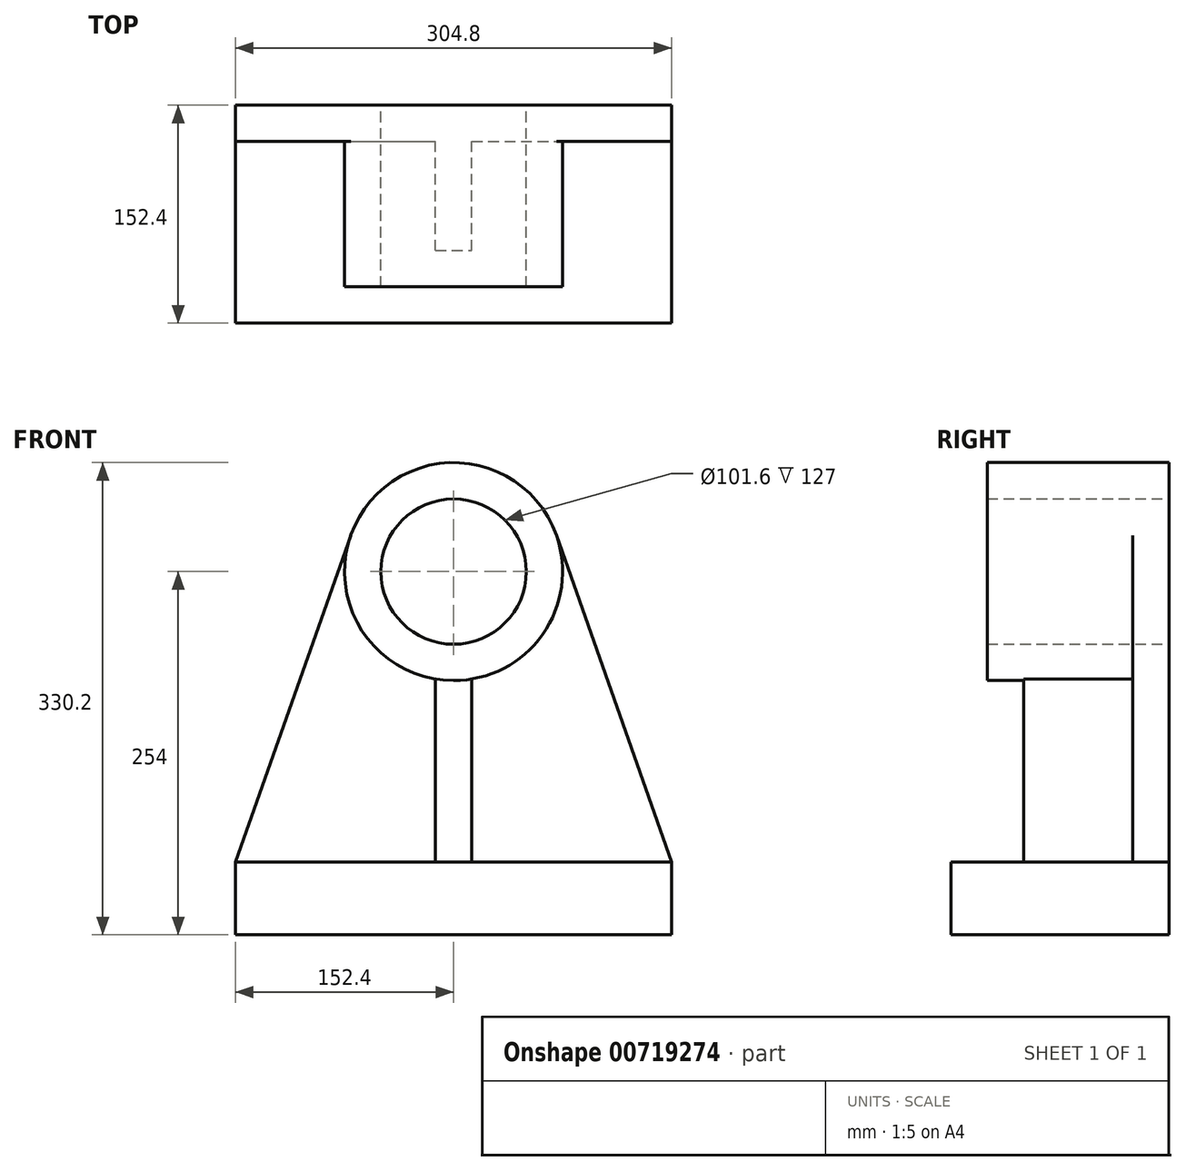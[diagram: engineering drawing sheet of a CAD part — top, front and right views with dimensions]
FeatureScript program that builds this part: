
annotation { "Feature Type Name" : "Feature", "Feature Type Description" : "" }
export const myFeature = defineFeature(function(context is Context, id is Id, definition is map)
    precondition{}
    {
        {
            var Q0;
            Q0=qCreatedBy(makeId("Front.planeOp"),FACE);
            var sketch = newSketch(context, id + "F0", { "sketchPlane" : qUnion([Q0])});
            skCircle(sketch, "E0", {"center": v(0, 0) * mm, "radius": 76.2 * mm});
            skCircle(sketch, "E1", {"center": v(0, 0) * mm, "radius": 50.8 * mm});
            skSolve(sketch);
        }
        {
            var Q0;
            Q0=makeQuery(id+"F0.imprint","IMPRINT",FACE,{"disambiguationData":[TD([[makeQuery(id+"F0.imprint","IMPRINT",EDGE,{"derivedFrom":sQuery(id+"F0.wireOp",EDGE,"E0")}),1.0]])]});
            extrude(context, id + "F1", {"entities" : qUnion([Q0]), "depth" : 127 * mm, "offsetDistance" : 25.4 * mm});
        }
        {
            var Q0;
            Q0=qCreatedBy(makeId("Front.planeOp"),FACE);
            var sketch = newSketch(context, id + "F2", { "sketchPlane" : qUnion([Q0])});
            skLineSegment(sketch, "E2", {"start": v(-71.87, 25.33) * mm, "end": v(-152.4, -203.2) * mm});
            skLineSegment(sketch, "E3", {"start": v(-152.4, -203.2) * mm, "end": v(152.4, -203.2) * mm});
            skLineSegment(sketch, "E4", {"start": v(152.4, -203.2) * mm, "end": v(71.87, 25.33) * mm});
            skLineSegment(sketch, "E5", {"start": v(0, 0) * mm, "end": v(0, -203.2) * mm});
            skArc(sketch, "E6", {"start": v(-71.87, 25.33) * mm, "mid": v(0, -76.2) * mm, "end": v(71.87, 25.33) * mm});
            skSolve(sketch);
        }
        {
            var Q0;
            {var subQ0=sQuery(id+"F2.wireOp",EDGE,"E2");Q0=makeQuery(id+"F2.imprint","IMPRINT",FACE,{"disambiguationData":[TD([[makeQuery(id+"F2.imprint","IMPRINT",EDGE,{"derivedFrom":subQ0}),1.0]])]});}
            var Q1;
            {var subQ0=sQuery(id+"F2.wireOp",EDGE,"E4");Q1=makeQuery(id+"F2.imprint","IMPRINT",FACE,{"disambiguationData":[TD([[makeQuery(id+"F2.imprint","IMPRINT",EDGE,{"derivedFrom":subQ0}),1.0]])]});}
            extrude(context, id + "F3", {"entities" : qUnion([Q0, Q1]), "operationType" : NewBodyOperationType.ADD, "depth" : 25.4 * mm, "offsetDistance" : 25.4 * mm});
        }
        {
            var Q0;
            Q0=makeQuery(id+"F3.boolean.opBoolean","MERGE",FACE,{"derivedFrom":[makeQuery(id+"F1.opExtrude","CAP_FACE",FACE,{"disambiguationData":[OSD([sQuery(id+"F0.wireOp",EDGE,"E0"),sQuery(id+"F0.wireOp",EDGE,"E1")])],"isStart":true}),makeQuery(id+"F3.opExtrude","CAP_FACE",FACE,{"disambiguationData":[OSD([sQuery(id+"F2.wireOp",EDGE,"E2"),sQuery(id+"F2.wireOp",EDGE,"E3"),sQuery(id+"F2.wireOp",EDGE,"E4"),sQuery(id+"F2.wireOp",EDGE,"E6")])],"isStart":true})]});
            var sketch = newSketch(context, id + "F4", { "sketchPlane" : qUnion([Q0])});
            skLineSegment(sketch, "E7.bottom", {"start": v(-152.4, -203.2) * mm, "end": v(152.4, -203.2) * mm});
            skLineSegment(sketch, "E7.top", {"start": v(-152.4, -254) * mm, "end": v(152.4, -254) * mm});
            skLineSegment(sketch, "E7.left", {"start": v(-152.4, -203.2) * mm, "end": v(-152.4, -254) * mm});
            skLineSegment(sketch, "E7.right", {"start": v(152.4, -203.2) * mm, "end": v(152.4, -254) * mm});
            skSolve(sketch);
        }
        {
            var Q0;
            Q0=makeQuery(id+"F4.imprint","IMPRINT",FACE,{"disambiguationData":[TD([[makeQuery(id+"F4.imprint","IMPRINT",EDGE,{"derivedFrom":sQuery(id+"F4.wireOp",EDGE,"E7.bottom")}),1.0]])]});
            extrude(context, id + "F5", {"entities" : qUnion([Q0]), "operationType" : NewBodyOperationType.ADD, "oppositeDirection" : true, "depth" : 152.4 * mm, "offsetDistance" : 25.4 * mm});
        }
        {
            var Q0;
            Q0=makeQuery(id+"F3.opExtrude","CAP_FACE",FACE,{"disambiguationData":[OSD([sQuery(id+"F2.wireOp",EDGE,"E2"),sQuery(id+"F2.wireOp",EDGE,"E3"),sQuery(id+"F2.wireOp",EDGE,"E4"),sQuery(id+"F2.wireOp",EDGE,"E6")])],"isStart":false});
            var sketch = newSketch(context, id + "F6", { "sketchPlane" : qUnion([Q0])});
            skLineSegment(sketch, "E8", {"start": v(0, 0) * mm, "end": v(0, -203.2) * mm});
            skLineSegment(sketch, "E9", {"start": v(-12.7, -75.13) * mm, "end": v(-12.7, -203.2) * mm});
            skLineSegment(sketch, "E10", {"start": v(-12.7, -203.2) * mm, "end": v(12.7, -203.2) * mm});
            skLineSegment(sketch, "E11", {"start": v(12.7, -203.2) * mm, "end": v(12.7, -75.13) * mm});
            skArc(sketch, "E12", {"start": v(-12.7, -75.13) * mm, "mid": v(0, -76.2) * mm, "end": v(12.7, -75.13) * mm});
            skSolve(sketch);
        }
        {
            var Q0;
            {var subQ5=sQuery(id+"F6.wireOp",EDGE,"E9");Q0=makeQuery(id+"F6.imprint","IMPRINT",FACE,{"disambiguationData":[TD([[makeQuery(id+"F6.imprint","IMPRINT",EDGE,{"derivedFrom":subQ5}),1.0]])]});}
            var Q1;
            {var subQ5=sQuery(id+"F6.wireOp",EDGE,"E11");Q1=makeQuery(id+"F6.imprint","IMPRINT",FACE,{"disambiguationData":[TD([[makeQuery(id+"F6.imprint","IMPRINT",EDGE,{"derivedFrom":subQ5}),1.0]])]});}
            extrude(context, id + "F7", {"entities" : qUnion([Q0, Q1]), "operationType" : NewBodyOperationType.ADD, "depth" : 76.2 * mm, "offsetDistance" : 25.4 * mm});
        }
    });
